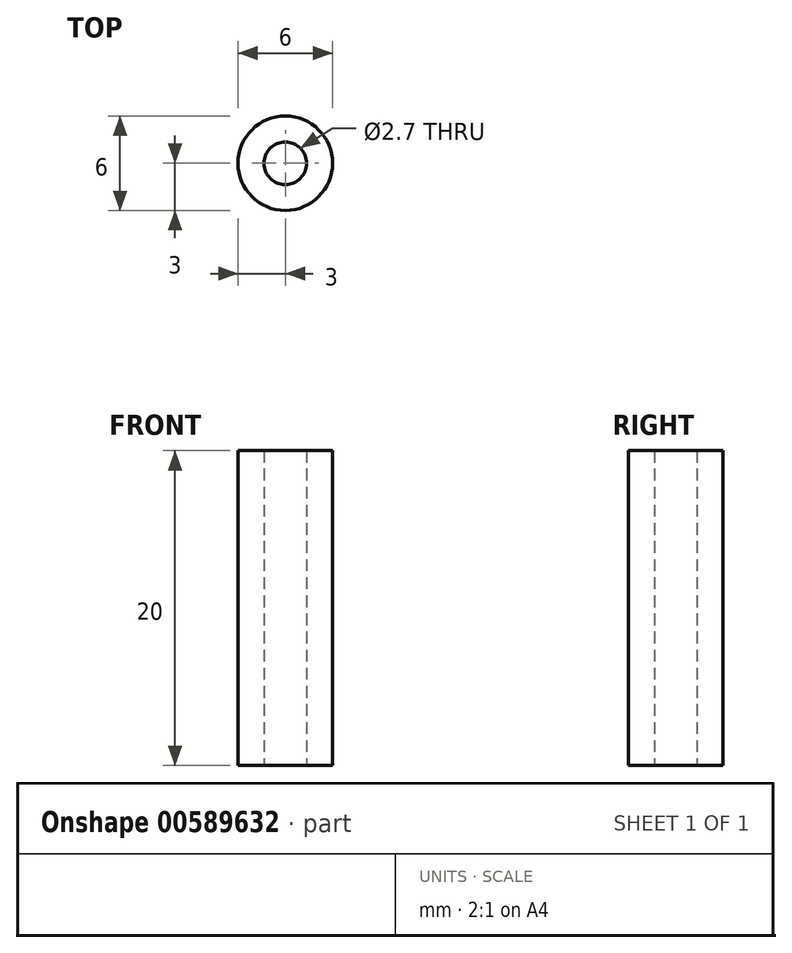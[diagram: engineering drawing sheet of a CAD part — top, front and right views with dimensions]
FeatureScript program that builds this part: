
annotation { "Feature Type Name" : "Feature", "Feature Type Description" : "" }
export const myFeature = defineFeature(function(context is Context, id is Id, definition is map)
    precondition{}
    {
        {
            var Q0;
            Q0=qCreatedBy(makeId("Top.planeOp"),FACE);
            var sketch = newSketch(context, id + "F0", { "sketchPlane" : qUnion([Q0])});
            skCircle(sketch, "E0", {"center": v(0, 0) * mm, "radius": 3 * mm});
            skCircle(sketch, "E1", {"center": v(0, 0) * mm, "radius": 1.35 * mm});
            skSolve(sketch);
        }
        {
            var Q0;
            Q0=makeQuery(id+"F0.imprint","IMPRINT",FACE,{"disambiguationData":[TD([[makeQuery(id+"F0.imprint","IMPRINT",EDGE,{"derivedFrom":sQuery(id+"F0.wireOp",EDGE,"E0")}),1.0]])]});
            extrude(context, id + "F1", {"entities" : qUnion([Q0]), "depth" : 20 * mm, "offsetDistance" : 25 * mm});
        }
    });
